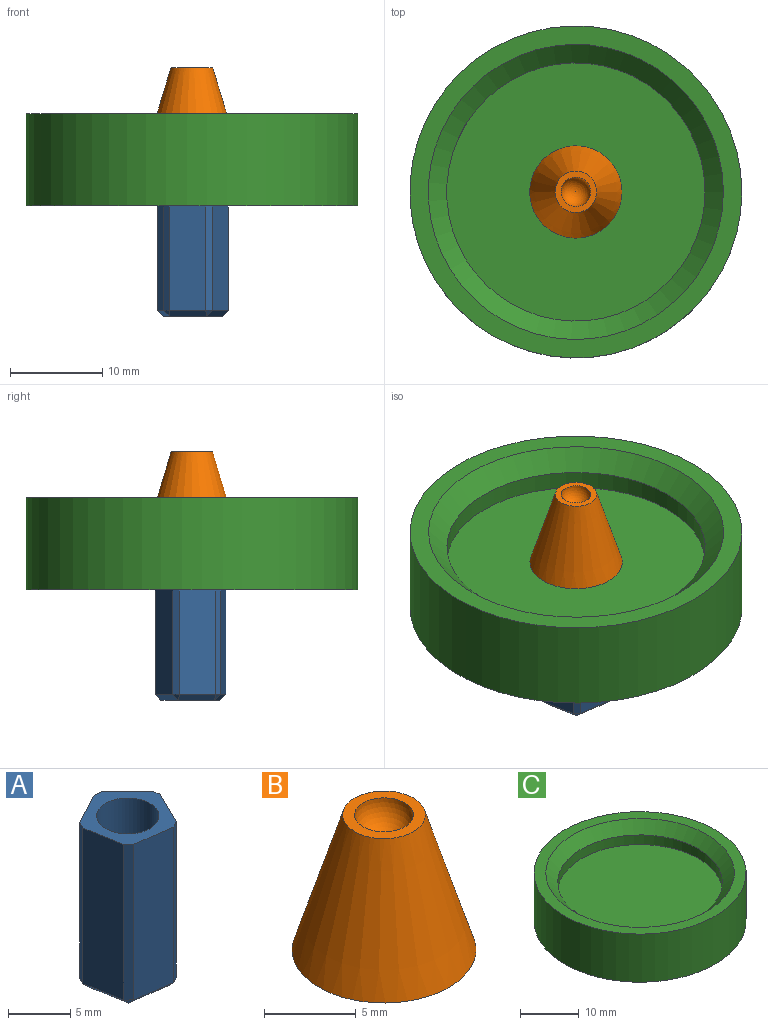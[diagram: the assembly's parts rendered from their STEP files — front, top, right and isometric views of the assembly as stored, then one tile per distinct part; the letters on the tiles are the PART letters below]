
ASSEMBLY  parts=3 mates=2
PART A: 23 faces, bbox 7.7x7.7x16 mm
  f0: plane 15.31x3.53mm, normal (-0.47,0.88,0), area 61.2mm2, adj f7,f8,f12,f13
  f1: plane 15.31x3.94mm, normal (-0.98,-0.18,0), area 61.2mm2, adj f7,f13,f18,f19
  f2: plane 15.31x3.96mm, normal (-0.14,-0.99,0), area 61.2mm2, adj f7,f16,f19,f22
  f3: plane 15.31x3.6mm, normal (0.9,-0.44,0), area 61.2mm2, adj f7,f10,f16,f17
  f4: plane 15.31x2.88mm, normal (0.69,0.72,0), area 61.2mm2, adj f7,f8,f10,f11
  f5: cylinder r=2.5mm len=16mm, axis (0,0,1), area 251.3mm2, adj f6,f7
  f6: plane 6.41x6.37mm, normal (0,0,-1), area 7.9mm2, adj f5,f11,f12,f17,f18,f22
  f7: plane 7.71x7.66mm, normal (0,0,1), area 22.8mm2, adj f0,f1,f2,f3,f4,f5,f8,f10
  f8: plane 15.31x0.8mm, normal (0.14,0.99,0), area 12.4mm2, adj f0,f4,f7,f9
  f9: plane 0.8x0.69mm, normal (0.11,0.77,-0.63), area 0.4mm2, adj f8,f11,f12
  f10: plane 15.31x0.8mm, normal (0.98,0.18,0), area 12.4mm2, adj f3,f4,f7,f14
  f11: plane 3.36x3.27mm, normal (0.49,0.51,-0.71), area 3.9mm2, adj f4,f6,f9,f14
  f12: plane 3.85x2.49mm, normal (-0.33,0.62,-0.71), area 3.9mm2, adj f0,f6,f9,f15
  f13: plane 15.31x0.73mm, normal (-0.9,0.44,0), area 12.4mm2, adj f0,f1,f7,f15
  f14: plane 0.8x0.69mm, normal (0.77,0.14,-0.63), area 0.4mm2, adj f10,f11,f17
  f15: plane 0.73x0.69mm, normal (-0.7,0.34,-0.63), area 0.4mm2, adj f12,f13,f18
  f16: plane 15.31x0.71mm, normal (0.47,-0.88,0), area 12.4mm2, adj f2,f3,f7,f20
  f17: plane 3.9x2.37mm, normal (0.64,-0.31,-0.71), area 3.9mm2, adj f3,f6,f14,f20
  f18: plane 4.06x1.38mm, normal (-0.7,-0.12,-0.71), area 3.9mm2, adj f1,f6,f15,f21
  f19: plane 15.31x0.58mm, normal (-0.69,-0.72,0), area 12.4mm2, adj f1,f2,f7,f21
  f20: plane 0.71x0.69mm, normal (0.37,-0.69,-0.63), area 0.4mm2, adj f16,f17,f22
  f21: plane 0.69x0.68mm, normal (-0.54,-0.56,-0.63), area 0.4mm2, adj f18,f19,f22
  f22: plane 4.06x1.23mm, normal (-0.1,-0.7,-0.71), area 3.9mm2, adj f2,f6,f20,f21
PART B: 4 faces, bbox 10x10x9 mm
  f0: cone r=5mm half-angle=17deg, axis (0,0,-1), area 214.3mm2, adj f1,f2
  f1: plane 4.5x4.5mm, normal (0,0,1), area 7.8mm2, adj f0,f3
  f2: plane 10x10mm, normal (0,0,-1), area 78.5mm2, adj f0
  f3: sphere r=1.6mm, area 16.1mm2, adj f1
PART C: 9 faces, bbox 36x36x10 mm
  f0: plane 36x36mm, normal (0,0,1), area 213.6mm2, adj f1,f8
  f1: cylinder r=18mm len=36mm, axis (0,0,1), area 1131mm2, adj f0,f2
  f2: plane 36x36mm, normal (0,0,-1), area 213.6mm2, adj f1,f7
  f3: cylinder r=14mm len=28mm, axis (0,0,1), area 175.9mm2, adj f4,f7
  f4: plane 28x28mm, normal (0,0,-1), area 615.8mm2, adj f3
  f5: plane 28x28mm, normal (0,0,1), area 615.8mm2, adj f6
  f6: cylinder r=14mm len=28mm, axis (0,0,1), area 175.9mm2, adj f5,f8
  f7: cone r=16mm half-angle=45deg, axis (0,0,-1), area 266.6mm2, adj f2,f3
  f8: cone r=14mm half-angle=45deg, axis (0,0,1), area 266.6mm2, adj f0,f6
PLACE A at identity
PLACE B t=(0,0,2)mm
PLACE C t=(0,0,4.04)mm
MATE fastened B.f0 <-> C.f1  axis (0,0,1) through (0,0,2)mm
MATE fastened C.f1 <-> A.f5  axis (0,0,-1) through (0,0,0)mm
